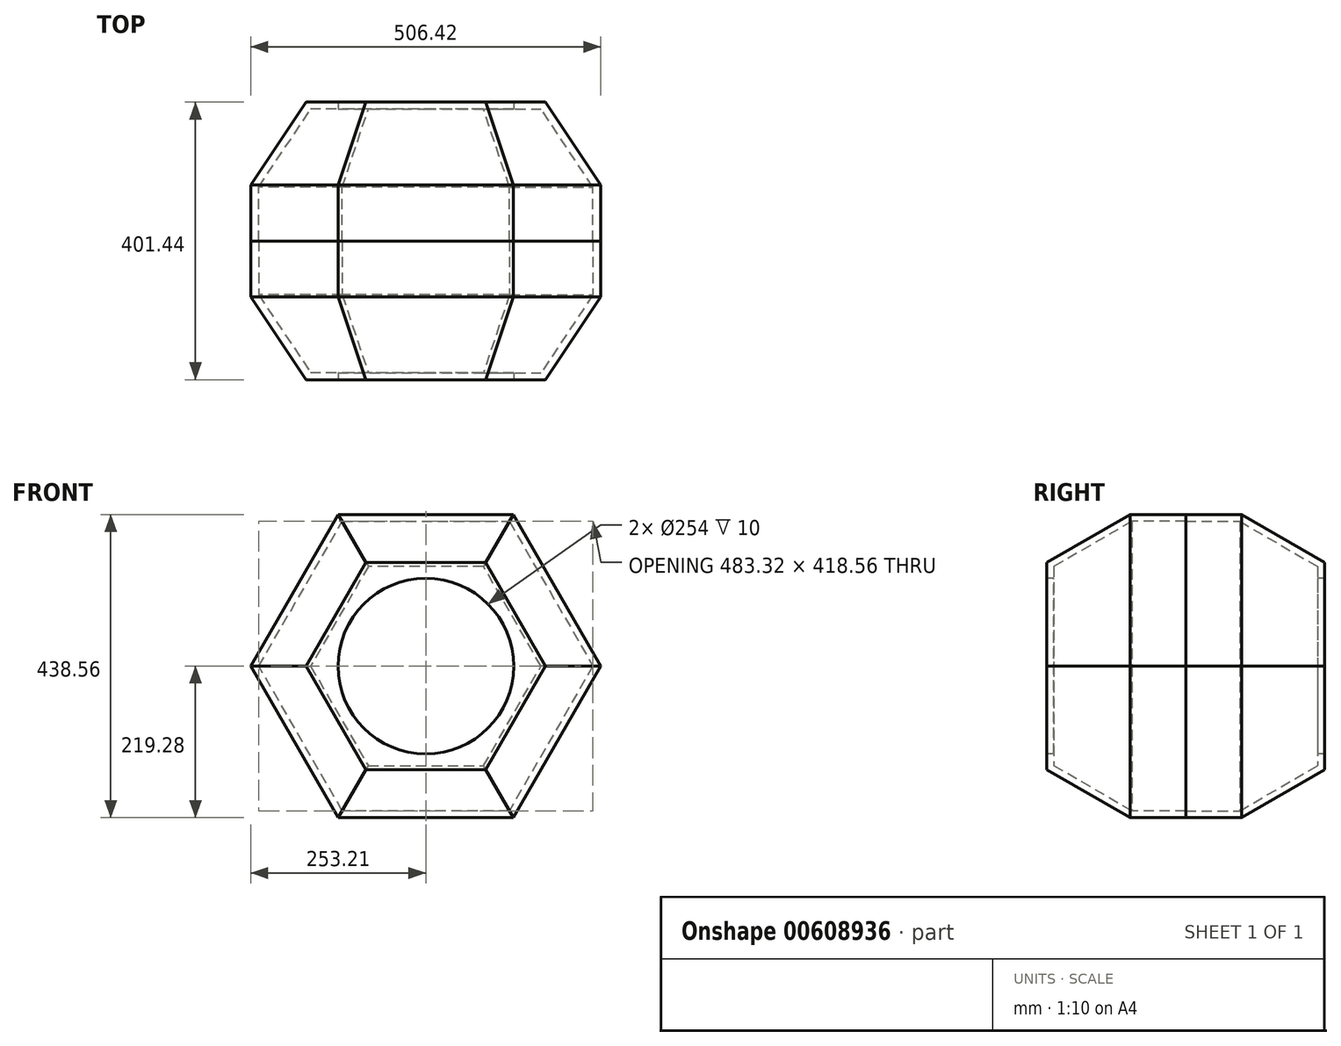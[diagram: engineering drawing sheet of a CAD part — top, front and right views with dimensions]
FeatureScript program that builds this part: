
annotation { "Feature Type Name" : "Feature", "Feature Type Description" : "" }
export const myFeature = defineFeature(function(context is Context, id is Id, definition is map)
    precondition{}
    {
        {
            var Q0;
            Q0=qCreatedBy(makeId("Front.planeOp"),FACE);
            var sketch = newSketch(context, id + "F0", { "sketchPlane" : qUnion([Q0])});
            skCircle(sketch, "E0.cCircle", {"center": v(0, 0) * mm, "radius": 150 * mm, "construction": true});
            skLineSegment(sketch, "E0.0", {"start": v(-86.6, 150) * mm, "end": v(86.6, 150) * mm});
            skLineSegment(sketch, "E0.1", {"start": v(86.6, 150) * mm, "end": v(173.2, 0) * mm});
            skLineSegment(sketch, "E0.2", {"start": v(173.2, 0) * mm, "end": v(86.6, -150) * mm});
            skLineSegment(sketch, "E0.3", {"start": v(86.6, -150) * mm, "end": v(-86.6, -150) * mm});
            skLineSegment(sketch, "E0.4", {"start": v(-86.6, -150) * mm, "end": v(-173.2, 0) * mm});
            skLineSegment(sketch, "E0.5", {"start": v(-173.2, 0) * mm, "end": v(-86.6, 150) * mm});
            skPoint(sketch, "E0.0.midPoint", {"position": v(0, 150) * mm});
            skSolve(sketch);
        }
        {
            var Q0;
            Q0=makeQuery(id+"F0.imprint","IMPRINT",FACE,{"disambiguationData":[TD([[makeQuery(id+"F0.imprint","IMPRINT",EDGE,{"derivedFrom":sQuery(id+"F0.wireOp",EDGE,"E0.0")}),-1.0]])]});
            extrude(context, id + "F1", {"entities" : qUnion([Q0]), "oppositeDirection" : true, "depth" : 120 * mm, "offsetDistance" : 25 * mm, "hasDraft" : true, "draftAngle" : 30 * degree});
        }
        {
            var Q0;
            Q0=makeQuery(id+"F1.opExtrude","CAP_FACE",FACE,{"disambiguationData":[OSD([sQuery(id+"F0.wireOp",EDGE,"E0.0"),sQuery(id+"F0.wireOp",EDGE,"E0.1"),sQuery(id+"F0.wireOp",EDGE,"E0.2"),sQuery(id+"F0.wireOp",EDGE,"E0.3"),sQuery(id+"F0.wireOp",EDGE,"E0.4"),sQuery(id+"F0.wireOp",EDGE,"E0.5")])],"isStart":false});
            extrude(context, id + "F2", {"entities" : qUnion([Q0]), "operationType" : NewBodyOperationType.ADD, "depth" : 80.72 * mm, "offsetDistance" : 25 * mm});
        }
        {
            var Q0;
            Q0=makeQuery(id+"F1.opExtrude","SWEPT_BODY",BODY,{"disambiguationData":[OSD([sQuery(id+"F0.wireOp",EDGE,"E0.0"),sQuery(id+"F0.wireOp",EDGE,"E0.1"),sQuery(id+"F0.wireOp",EDGE,"E0.2"),sQuery(id+"F0.wireOp",EDGE,"E0.3"),sQuery(id+"F0.wireOp",EDGE,"E0.4"),sQuery(id+"F0.wireOp",EDGE,"E0.5")])]});
            var Q1;
            Q1=makeQuery(id+"F2.opExtrude","CAP_FACE",FACE,{"disambiguationData":[OSD([sQuery(id+"F0.wireOp",EDGE,"E0.0"),sQuery(id+"F0.wireOp",EDGE,"E0.1"),sQuery(id+"F0.wireOp",EDGE,"E0.2"),sQuery(id+"F0.wireOp",EDGE,"E0.3"),sQuery(id+"F0.wireOp",EDGE,"E0.4"),sQuery(id+"F0.wireOp",EDGE,"E0.5")])],"isStart":false});
            mirror(context, id + "F3", {"entities" : qUnion([Q0]), "mirrorPlane" : qUnion([Q1])});
        }
        {
            var Q0;
            Q0=makeQuery(id+"F2.opExtrude","CAP_FACE",FACE,{"disambiguationData":[OSD([sQuery(id+"F0.wireOp",EDGE,"E0.0"),sQuery(id+"F0.wireOp",EDGE,"E0.1"),sQuery(id+"F0.wireOp",EDGE,"E0.2"),sQuery(id+"F0.wireOp",EDGE,"E0.3"),sQuery(id+"F0.wireOp",EDGE,"E0.4"),sQuery(id+"F0.wireOp",EDGE,"E0.5")])],"isStart":false});
            shell(context, id + "F4", {"entities" : qUnion([Q0]), "thickness" : 10 * mm});
        }
        {
            var Q0;
            Q0=makeQuery(id+"F3.opPattern","COPY",FACE,{"derivedFrom":makeQuery(id+"F2.opExtrude","CAP_FACE",FACE,{"disambiguationData":[OSD([sQuery(id+"F0.wireOp",EDGE,"E0.0"),sQuery(id+"F0.wireOp",EDGE,"E0.1"),sQuery(id+"F0.wireOp",EDGE,"E0.2"),sQuery(id+"F0.wireOp",EDGE,"E0.3"),sQuery(id+"F0.wireOp",EDGE,"E0.4"),sQuery(id+"F0.wireOp",EDGE,"E0.5")])],"isStart":false}),"instanceName":"1"});
            shell(context, id + "F5", {"entities" : qUnion([Q0]), "thickness" : 10 * mm});
        }
        {
            var Q0;
            Q0=makeQuery(id+"F1.opExtrude","CAP_FACE",FACE,{"disambiguationData":[OSD([sQuery(id+"F0.wireOp",EDGE,"E0.0"),sQuery(id+"F0.wireOp",EDGE,"E0.1"),sQuery(id+"F0.wireOp",EDGE,"E0.2"),sQuery(id+"F0.wireOp",EDGE,"E0.3"),sQuery(id+"F0.wireOp",EDGE,"E0.4"),sQuery(id+"F0.wireOp",EDGE,"E0.5")])],"isStart":true});
            var sketch = newSketch(context, id + "F6", { "sketchPlane" : qUnion([Q0])});
            skCircle(sketch, "E1", {"center": v(0, 0) * mm, "radius": 127 * mm});
            skSolve(sketch);
        }
        {
            var Q0;
            Q0 = qSketchRegion(id + "F6", true);
            extrude(context, id + "F7", {"entities" : qUnion([Q0]), "operationType" : NewBodyOperationType.REMOVE, "endBound" : BoundingType.THROUGH_ALL, "oppositeDirection" : true, "depth" : 25 * mm, "offsetDistance" : 25 * mm});
        }
    });
